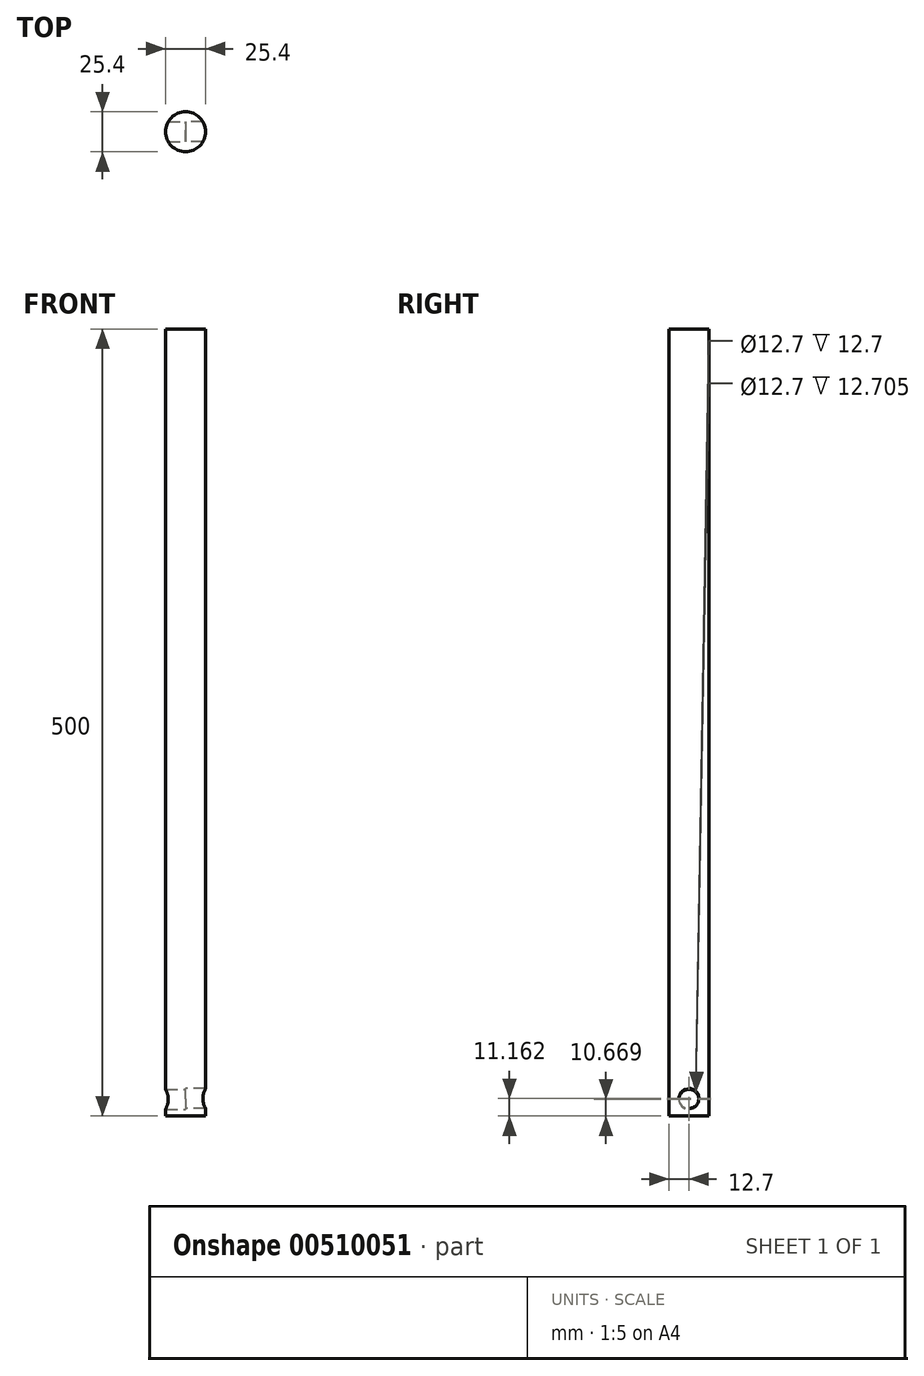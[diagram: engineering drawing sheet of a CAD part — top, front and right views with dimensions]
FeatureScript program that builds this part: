
annotation { "Feature Type Name" : "Feature", "Feature Type Description" : "" }
export const myFeature = defineFeature(function(context is Context, id is Id, definition is map)
    precondition{}
    {
        {
            var Q0;
            Q0=qCreatedBy(makeId("Top.planeOp"),FACE);
            var sketch = newSketch(context, id + "F0", { "sketchPlane" : qUnion([Q0])});
            skCircle(sketch, "E0", {"center": v(0, 0) * mm, "radius": 12.7 * mm});
            skSolve(sketch);
        }
        {
            var Q0;
            Q0=qSketchRegion(id+"F0",true);
            extrude(context, id + "F1", {"entities" : qUnion([Q0]), "depth" : 500 * mm});
        }
        {
            var Q0;
            Q0=qCreatedBy(makeId("Right.planeOp"),FACE);
            var sketch = newSketch(context, id + "F2", { "sketchPlane" : qUnion([Q0])});
            skCircle(sketch, "E1", {"center": v(0, 11.16) * mm, "radius": 6.35 * mm});
            skSolve(sketch);
        }
        {
            var Q0;
            Q0=qSketchRegion(id+"F2",true);
            extrude(context, id + "F3", {"entities" : qUnion([Q0]), "operationType" : NewBodyOperationType.REMOVE, "depth" : 76.2 * mm});
        }
        {
            var Q0;
            Q0=qCreatedBy(makeId("Right.planeOp"),FACE);
            var sketch = newSketch(context, id + "F4", { "sketchPlane" : qUnion([Q0])});
            skCircle(sketch, "E2", {"center": v(0, 10.67) * mm, "radius": 6.35 * mm});
            skSolve(sketch);
        }
        {
            var Q0;
            Q0=qSketchRegion(id+"F4",true);
            extrude(context, id + "F5", {"entities" : qUnion([Q0]), "operationType" : NewBodyOperationType.REMOVE, "oppositeDirection" : true, "depth" : 76.2 * mm});
        }
    });
